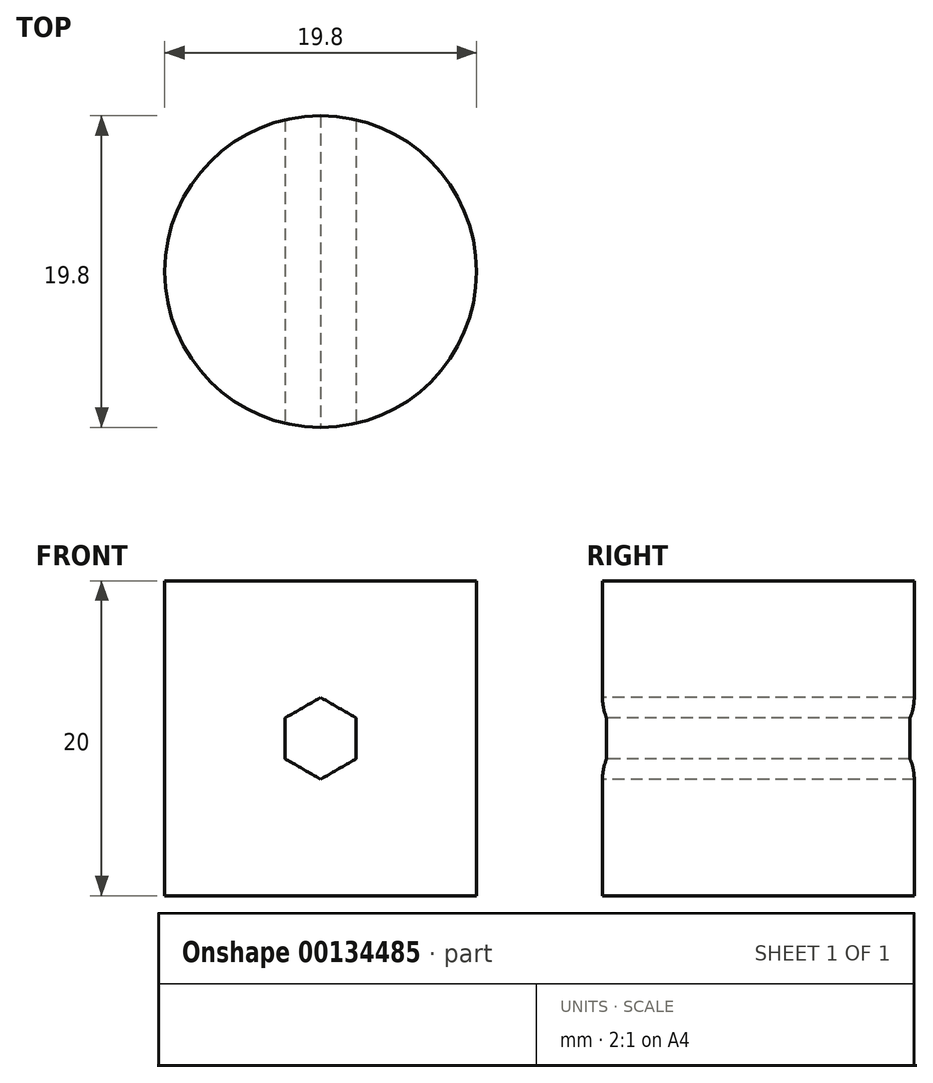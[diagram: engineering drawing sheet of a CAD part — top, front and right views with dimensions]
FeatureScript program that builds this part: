
annotation { "Feature Type Name" : "Feature", "Feature Type Description" : "" }
export const myFeature = defineFeature(function(context is Context, id is Id, definition is map)
    precondition{}
    {
        {
            var Q0;
            Q0=qCreatedBy(makeId("Top.planeOp"),FACE);
            var sketch = newSketch(context, id + "F0", { "sketchPlane" : qUnion([Q0])});
            skCircle(sketch, "E0", {"center": v(0, 0) * mm, "radius": 9.9 * mm});
            skSolve(sketch);
        }
        {
            var Q0;
            Q0 = qSketchRegion(id + "F0", true);
            extrude(context, id + "F1", {"entities" : qUnion([Q0]), "depth" : 20 * mm});
        }
        {
            var Q0;
            Q0=qCreatedBy(makeId("Front.planeOp"),FACE);
            var sketch = newSketch(context, id + "F2", { "sketchPlane" : qUnion([Q0])});
            skCircle(sketch, "E1.cCircle", {"center": v(0, 10) * mm, "radius": 2.25 * mm, "construction": true});
            skLineSegment(sketch, "E1.0", {"start": v(2.25, 11.3) * mm, "end": v(2.25, 8.7) * mm});
            skLineSegment(sketch, "E1.1", {"start": v(2.25, 8.7) * mm, "end": v(0, 7.4) * mm});
            skLineSegment(sketch, "E1.2", {"start": v(0, 7.4) * mm, "end": v(-2.25, 8.7) * mm});
            skLineSegment(sketch, "E1.3", {"start": v(-2.25, 8.7) * mm, "end": v(-2.25, 11.3) * mm});
            skLineSegment(sketch, "E1.4", {"start": v(-2.25, 11.3) * mm, "end": v(0, 12.6) * mm});
            skLineSegment(sketch, "E1.5", {"start": v(0, 12.6) * mm, "end": v(2.25, 11.3) * mm});
            skPoint(sketch, "E1.0.midPoint", {"position": v(2.25, 10) * mm});
            skSolve(sketch);
        }
        {
            var Q0;
            Q0 = qSketchRegion(id + "F2", true);
            extrude(context, id + "F3", {"entities" : qUnion([Q0]), "operationType" : NewBodyOperationType.REMOVE, "endBound" : BoundingType.THROUGH_ALL, "oppositeDirection" : true, "depth" : 25 * mm, "hasSecondDirection" : true, "secondDirectionBound" : BoundingType.THROUGH_ALL, "secondDirectionOppositeDirection" : false, "secondDirectionDepth" : 25 * mm});
        }
    });
